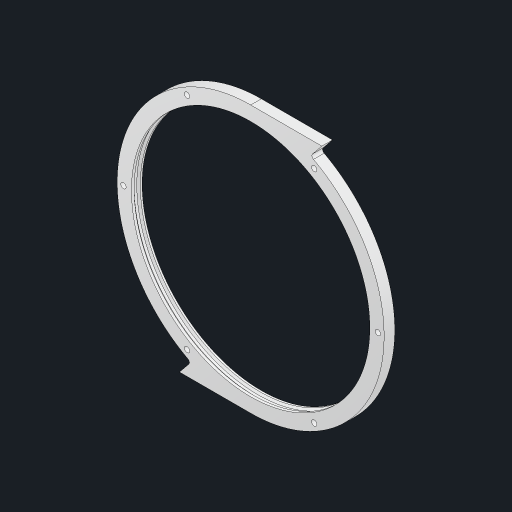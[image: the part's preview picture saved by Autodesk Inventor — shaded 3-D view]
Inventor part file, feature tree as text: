
AUTODESK INVENTOR PART (.ipt)
format: ipt  version: 2023.2 (Build 272271030, 271C)  size: 180,736 bytes
history: native  units: mm
features: sketch x4, extrude x4, pattern_circular x2, revolve x1, fillet x1
ambient origin geometry x8: Origin, YZ Plane, XZ Plane, XY Plane, X Axis, Y Axis, Z Axis, Center Point
bodies: Solid1 (feature_tree)
feature tree (12):
  sketch  "Sketch1"  dims[d0=134.0mm d1=150.0mm]
  extrude  "Extrusion1"  Depth=150.0mm
  extrude  "Extrusion2"  Depth=1.6mm
  revolve  "Revolution1"  [1 undecoded]
  extrude  "Extrusion3"  Depth=6.0mm
  extrude  "Extrusion4"  Depth=6.0mm TaperAngle=0.0deg
  fillet  "Fillet1"  Radius=5.0mm
  pattern_circular  "Circular Pattern1"  [2 undecoded]
  pattern_circular  "Circular Pattern2"  Count=6 Angle=360.0deg
  sketch  "Sketch2"  dims[d2=10.0mm d3=1.6mm]
  sketch  "Sketch3"  dims[d4=20.0mm d6=360.0deg d8=6.0mm d9=0.0mm]
  sketch  "Sketch4"  dims[d10=6.0mm d11=0.0mm d12=3.0mm d15=5.0mm d16=0.0mm d17=5.0mm d18=0.0mm d19=4.0mm d20=60.0mm d21=360.0deg d24=6.0mm d25=2.5mm d27=1.0mm d28=0.5mm d29=0.5mm d30=90.0deg d31=20.0mm d32=360.0deg]
note: 3 required parameter values undecoded (feature->parameter linkage not recoverable at this tier; creation-order binding heuristic only, values carry confidence <= 0.55)